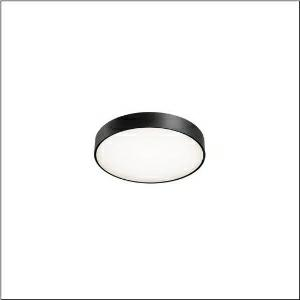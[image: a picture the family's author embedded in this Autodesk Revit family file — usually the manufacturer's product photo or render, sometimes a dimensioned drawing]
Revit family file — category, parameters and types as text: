
# Revit family: round_21_s_51mr34fd0421b
name_source: partatom
category: Lighting Fixtures
units: mm (PartAtom-declared; Revit-internal decimal feet)

## family parameters
Cut with Voids When Loaded = No
Host = Face
Light Source = No
Part Type = Normal
Room Calculation Point = No
Round Connector Dimension = Use Diameter
Shared = No

## types (1)
- Round 21 S (1 x LED, 3910 lm, 30.3 W, 4000K)
    Apparent Load = 30 VA
    CIE Flux Codes = 49 80 96 100 100
    Color Rendering = 80
    Color Temperature = 4000K
    Default Elevation = 1800 mm
    Description = Round 21 S, wall and ceiling luminaire, primary optical cover: cover, of PMMA, opal, light emission: direct distribution, primary light characteristic: symmetric, installation type: suspended mounting, surface-mounted, LED, rated luminous flux: 3.900lm, luminous efficacy: 129lm/W, light colour: 840, colour temperature: 4000K, control gear: DALI 2, with terminal, 5-pole, mains connection: 230V, AC, 50/60Hz, rated input power: 30.3W, housing, of aluminium, coated, black, diameter: 400mm, height: 62mm, protection rating (complete): IP40, insulation class (complete): insulation class I (protective earthing), certification: CE, impact resistance: IK04, permissible operating ambient temperature: -10..+35°C, packaging unit: 1 piece
    Height = 87 mm
    Lamp = 1 x LED
    Lamp Light Flux = 3910 lm
    Lamp Power = 30.3 W
    Lamp count = 1
    Length = 400 mm
    Luminous efficacy = 129 lm/W
    Manufacturer = Siteco
    ModVariant = No
    Model = 51MR34FD0421B
    Mounting Place = Ceiling
    Mounting Type = Surface mounted
    Number of Poles = 1
    OnlyDefault = Yes
    Power Factor = 1
    Product Name = Round 21 S
    Product group = wall and ceiling luminaire
    ProductGroupID = 304
    Protection Class = Protection class I
    Protection Degree = IP 40
    RLX_Detail_Level = 1
    RLX_Emergency_Light_Flux = 0 lm
    RLX_Emergency_Type = 0
    RLX_Emergency_Type_DB = No
    RlxData = <blob elided: 13449 chars, md5=932d72ad>
    Socket = socket
    Standby Power = 0 W
    System Light Flux = 3910 lm
    System Power = 30 W
    Type Comments = Product without accessories
    Type Image = l_1258311.jpg
    URL = http://relux.com
    VarID = ---
    Voltage = 0 V
    Weight = 0.00 kg
    Width = 0 mm  [stored 0 ft]

note: [stored X ft] marks values corroborated as IEEE doubles in the binary element streams (Revit-internal decimal feet)

## geometry (parser evidence)
native form markers: Sweep x9
no freeform markers — native parametric forms only
